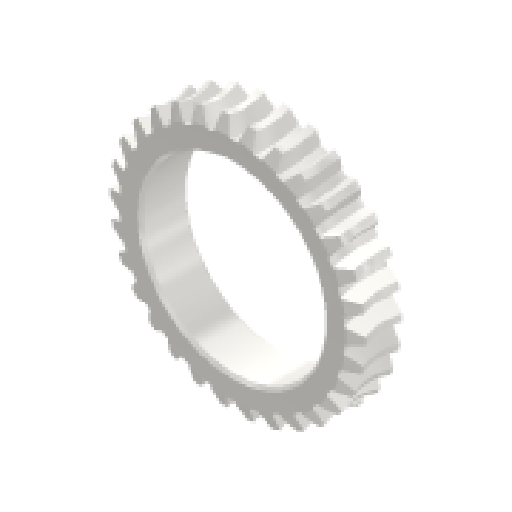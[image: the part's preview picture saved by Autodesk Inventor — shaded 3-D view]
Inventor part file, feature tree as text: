
AUTODESK INVENTOR PART (.ipt)
format: ipt  version: 2024.1 (Build 281209000, 209)  size: 538,112 bytes
history: native  units: mm (DEFAULTED — no unit token found)
features: other x10, plane x3, pattern_circular x1, extrude x1, chamfer x1, sketch x1, reference x1
ambient origin geometry x5: Origin, X Axis, Y Axis, Z Axis, Center Point
bodies: Solid1 (feature_tree)
feature tree (18):
  other  "Zahnebene"
  other  "Grundkörperskizze"
  other  "Grundkörper"
  other  "Grundkörper2"
  plane  "Work Plane13"
  other  "Zahn"
  pattern_circular  "Zahnanordnung"  [2 undecoded]
  plane  "Work Plane14"
  plane  "Work Plane15"
  extrude  "Extrusion1"  Depth=10.0mm
  chamfer  "Fasen1"  Distance=3.490659mm
  other  "Zahnskizze"
  other  "Srf1"
  sketch  "Skizze9"  dims[d35=90.0deg d37=-0.665682mm d38=28.975mm d39=3.490659mm d40=7.875mm d41=9.375mm d42=1.3mm d43=90.0deg d44=300.0mm d46=360.0deg d50=3.859836mm d68=28.975mm d69=0.0mm d73=0.0mm d75=1.047198mm d77=37.5mm d78=8.0mm d79=0.0mm d80=0.0mm d81=0.0mm d82=0.0mm d83=1.047198mm d84=0.0mm d85=180.0deg d86=28.975mm d87=42.95mm d89=16.25mm d90=90.0deg d92=8.0mm d93=28.975mm d94=0.3mm d95=10.0mm d96=0.0mm d97=0.5mm d98=2.0mm d99=45.0deg d100=30.7mm]
  reference  "Referenz1"
  other  "Flankendurchmesser"
  other  "Assembly_Planktoscope_Uc2version_wormdrive_V3.iam"
  other  "00_CCTV_Lens_Hikvision_50mm_2.8:1"
note: 2 required parameter values undecoded (feature->parameter linkage not recoverable at this tier; creation-order binding heuristic only, values carry confidence <= 0.55)
